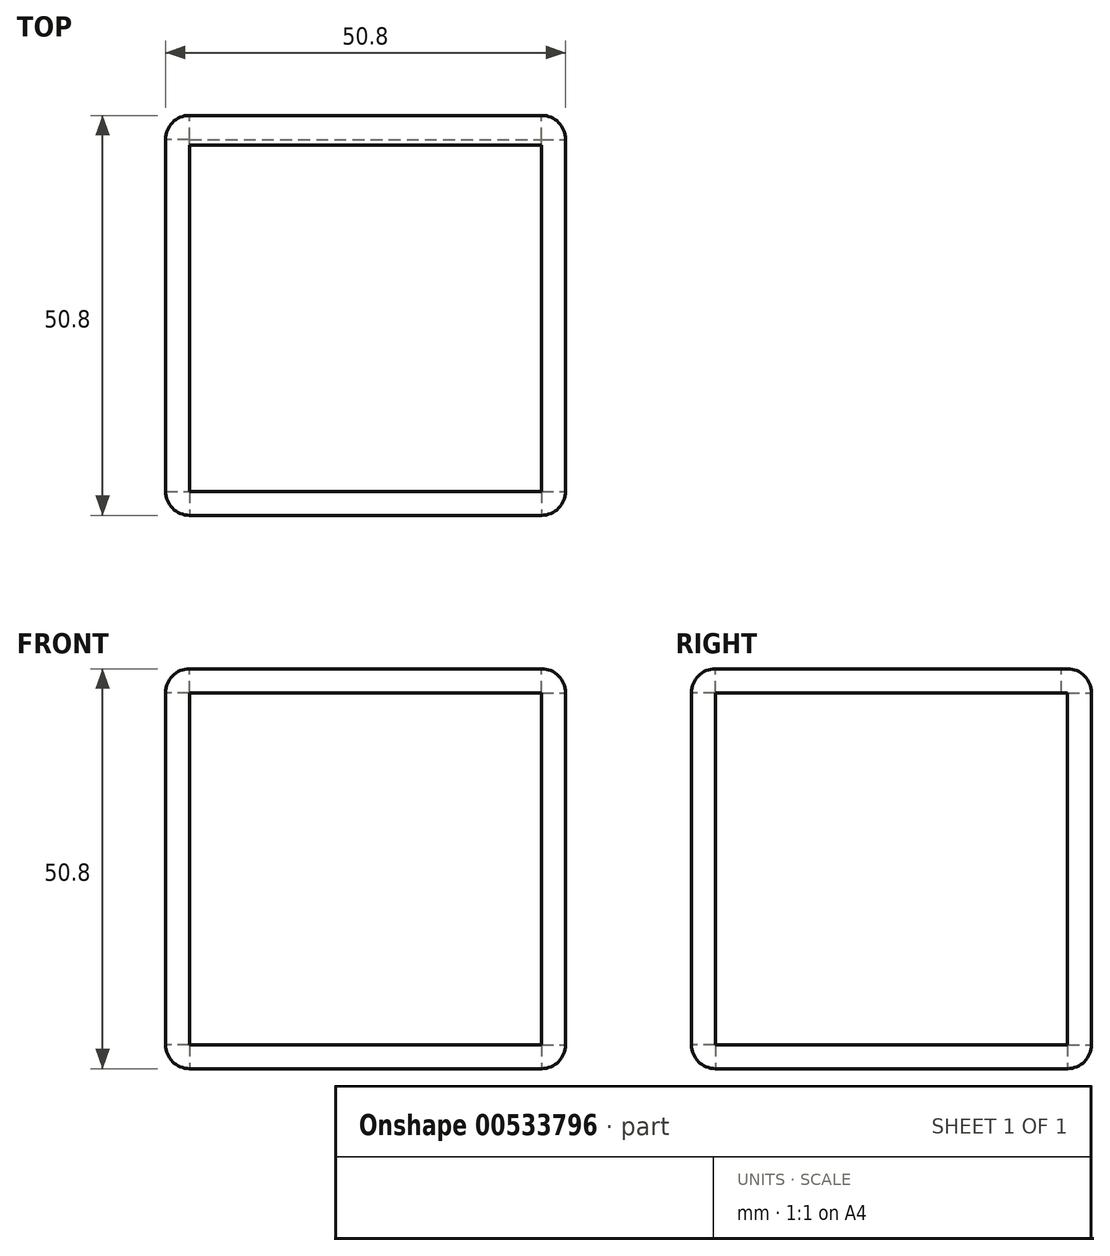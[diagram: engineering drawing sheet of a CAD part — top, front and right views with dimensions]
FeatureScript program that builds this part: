
annotation { "Feature Type Name" : "Feature", "Feature Type Description" : "" }
export const myFeature = defineFeature(function(context is Context, id is Id, definition is map)
    precondition{}
    {
        {
            var Q0;
            Q0=qCreatedBy(makeId("Top.planeOp"),FACE);
            var sketch = newSketch(context, id + "F0", { "sketchPlane" : qUnion([Q0])});
            skLineSegment(sketch, "E0.bottom", {"start": v(0, 0) * mm, "end": v(50.8, 0) * mm});
            skLineSegment(sketch, "E0.top", {"start": v(0, 50.8) * mm, "end": v(50.8, 50.8) * mm});
            skLineSegment(sketch, "E0.left", {"start": v(0, 0) * mm, "end": v(0, 50.8) * mm});
            skLineSegment(sketch, "E0.right", {"start": v(50.8, 0) * mm, "end": v(50.8, 50.8) * mm});
            skLineSegment(sketch, "E1.0", {"start": v(3.05, 47.75) * mm, "end": v(47.75, 47.75) * mm});
            skLineSegment(sketch, "E1.1", {"start": v(3.05, 3.05) * mm, "end": v(3.05, 47.75) * mm});
            skLineSegment(sketch, "E1.2", {"start": v(3.05, 3.05) * mm, "end": v(47.75, 3.05) * mm});
            skLineSegment(sketch, "E1.3", {"start": v(47.75, 3.05) * mm, "end": v(47.75, 47.75) * mm});
            skSolve(sketch);
        }
        {
            var Q0;
            Q0=qCreatedBy(makeId("Front.planeOp"),FACE);
            var sketch = newSketch(context, id + "F1", { "sketchPlane" : qUnion([Q0])});
            skLineSegment(sketch, "E2.bottom", {"start": v(0, 0) * mm, "end": v(50.8, 0) * mm});
            skLineSegment(sketch, "E2.top", {"start": v(0, 50.8) * mm, "end": v(50.8, 50.8) * mm});
            skLineSegment(sketch, "E2.left", {"start": v(0, 0) * mm, "end": v(0, 50.8) * mm});
            skLineSegment(sketch, "E2.right", {"start": v(50.8, 0) * mm, "end": v(50.8, 50.8) * mm});
            skLineSegment(sketch, "E3.0", {"start": v(3.05, 47.75) * mm, "end": v(47.75, 47.75) * mm});
            skLineSegment(sketch, "E3.1", {"start": v(3.05, 3.05) * mm, "end": v(3.05, 47.75) * mm});
            skLineSegment(sketch, "E3.2", {"start": v(3.05, 3.05) * mm, "end": v(47.75, 3.05) * mm});
            skLineSegment(sketch, "E3.3", {"start": v(47.75, 3.05) * mm, "end": v(47.75, 47.75) * mm});
            skSolve(sketch);
        }
        {
            var Q0;
            Q0=qCreatedBy(makeId("Right.planeOp"),FACE);
            var sketch = newSketch(context, id + "F2", { "sketchPlane" : qUnion([Q0])});
            skLineSegment(sketch, "E4.bottom", {"start": v(0, 0) * mm, "end": v(50.8, 0) * mm});
            skLineSegment(sketch, "E4.top", {"start": v(0, 50.8) * mm, "end": v(50.8, 50.8) * mm});
            skLineSegment(sketch, "E4.left", {"start": v(0, 0) * mm, "end": v(0, 50.8) * mm});
            skLineSegment(sketch, "E4.right", {"start": v(50.8, 0) * mm, "end": v(50.8, 50.8) * mm});
            skLineSegment(sketch, "E5.0", {"start": v(3.05, 47.75) * mm, "end": v(47.75, 47.75) * mm});
            skLineSegment(sketch, "E5.1", {"start": v(3.05, 3.05) * mm, "end": v(3.05, 47.75) * mm});
            skLineSegment(sketch, "E5.2", {"start": v(3.05, 3.05) * mm, "end": v(47.75, 3.05) * mm});
            skLineSegment(sketch, "E5.3", {"start": v(47.75, 3.05) * mm, "end": v(47.75, 47.75) * mm});
            skSolve(sketch);
        }
        {
            var Q0;
            Q0=makeQuery(id+"F2.imprint","IMPRINT",FACE,{"disambiguationData":[TD([[makeQuery(id+"F2.imprint","IMPRINT",EDGE,{"derivedFrom":sQuery(id+"F2.wireOp",EDGE,"E5.0")}),-1.0]])]});
            cPlane(context, id + "F3", {"entities" : qUnion([Q0]), "cplaneType" : CPlaneType.OFFSET, "offset" : 50.8 * mm, "width" : 152.4 * mm, "height" : 152.4 * mm});
        }
        {
            var Q0;
            Q0=makeQuery(id+"F1.imprint","IMPRINT",FACE,{"disambiguationData":[TD([[makeQuery(id+"F1.imprint","IMPRINT",EDGE,{"derivedFrom":sQuery(id+"F1.wireOp",EDGE,"E3.0")}),-1.0]])]});
            cPlane(context, id + "F4", {"entities" : qUnion([Q0]), "cplaneType" : CPlaneType.OFFSET, "offset" : 50.8 * mm, "oppositeDirection" : true, "width" : 152.4 * mm, "height" : 152.4 * mm});
        }
        {
            var Q0;
            Q0=makeQuery(id+"F0.imprint","IMPRINT",FACE,{"disambiguationData":[TD([[makeQuery(id+"F0.imprint","IMPRINT",EDGE,{"derivedFrom":sQuery(id+"F0.wireOp",EDGE,"E1.0")}),-1.0]])]});
            cPlane(context, id + "F5", {"entities" : qUnion([Q0]), "cplaneType" : CPlaneType.OFFSET, "offset" : 50.8 * mm, "width" : 152.4 * mm, "height" : 152.4 * mm});
        }
        {
            var Q0;
            Q0=qCreatedBy(id+"F3.planeOp",FACE);
            var sketch = newSketch(context, id + "F6", { "sketchPlane" : qUnion([Q0])});
            skLineSegment(sketch, "E6.bottom", {"start": v(0, 0) * mm, "end": v(50.8, 0) * mm});
            skLineSegment(sketch, "E6.top", {"start": v(0, 50.8) * mm, "end": v(50.8, 50.8) * mm});
            skLineSegment(sketch, "E6.left", {"start": v(0, 0) * mm, "end": v(0, 50.8) * mm});
            skLineSegment(sketch, "E6.right", {"start": v(50.8, 0) * mm, "end": v(50.8, 50.8) * mm});
            skLineSegment(sketch, "E7.0", {"start": v(3.05, 47.75) * mm, "end": v(47.75, 47.75) * mm});
            skLineSegment(sketch, "E7.1", {"start": v(3.05, 3.05) * mm, "end": v(3.05, 47.75) * mm});
            skLineSegment(sketch, "E7.2", {"start": v(3.05, 3.05) * mm, "end": v(47.75, 3.05) * mm});
            skLineSegment(sketch, "E7.3", {"start": v(47.75, 3.05) * mm, "end": v(47.75, 47.75) * mm});
            skSolve(sketch);
        }
        {
            var Q0;
            Q0=qCreatedBy(id+"F4.planeOp",FACE);
            var sketch = newSketch(context, id + "F7", { "sketchPlane" : qUnion([Q0])});
            skLineSegment(sketch, "E8.bottom", {"start": v(0, 0) * mm, "end": v(50.8, 0) * mm});
            skLineSegment(sketch, "E8.top", {"start": v(0, 50.8) * mm, "end": v(50.8, 50.8) * mm});
            skLineSegment(sketch, "E8.left", {"start": v(0, 0) * mm, "end": v(0, 50.8) * mm});
            skLineSegment(sketch, "E8.right", {"start": v(50.8, 0) * mm, "end": v(50.8, 50.8) * mm});
            skLineSegment(sketch, "E9.0", {"start": v(3.05, 47.75) * mm, "end": v(47.75, 47.75) * mm});
            skLineSegment(sketch, "E9.1", {"start": v(3.05, 3.05) * mm, "end": v(3.05, 47.75) * mm});
            skLineSegment(sketch, "E9.2", {"start": v(3.05, 3.05) * mm, "end": v(47.75, 3.05) * mm});
            skLineSegment(sketch, "E9.3", {"start": v(47.75, 3.05) * mm, "end": v(47.75, 47.75) * mm});
            skSolve(sketch);
        }
        {
            var Q0;
            Q0=qCreatedBy(id+"F5.planeOp",FACE);
            var sketch = newSketch(context, id + "F8", { "sketchPlane" : qUnion([Q0])});
            skLineSegment(sketch, "E10.bottom", {"start": v(0, 0) * mm, "end": v(50.8, 0) * mm});
            skLineSegment(sketch, "E10.top", {"start": v(0, 50.04) * mm, "end": v(50.8, 50.04) * mm});
            skLineSegment(sketch, "E10.left", {"start": v(0, 0) * mm, "end": v(0, 50.04) * mm});
            skLineSegment(sketch, "E10.right", {"start": v(50.8, 0) * mm, "end": v(50.8, 50.04) * mm});
            skLineSegment(sketch, "E11.0", {"start": v(3.05, 3.05) * mm, "end": v(47.75, 3.05) * mm});
            skLineSegment(sketch, "E11.1", {"start": v(3.05, 3.05) * mm, "end": v(3.05, 47) * mm});
            skLineSegment(sketch, "E11.2", {"start": v(3.05, 47) * mm, "end": v(47.75, 47) * mm});
            skLineSegment(sketch, "E11.3", {"start": v(47.75, 3.05) * mm, "end": v(47.75, 47) * mm});
            skSolve(sketch);
        }
        {
            var Q0;
            Q0=makeQuery(id+"F0.imprint","IMPRINT",FACE,{"disambiguationData":[TD([[makeQuery(id+"F0.imprint","IMPRINT",EDGE,{"derivedFrom":sQuery(id+"F0.wireOp",EDGE,"E0.bottom")}),1.0]])]});
            extrude(context, id + "F9", {"entities" : qUnion([Q0]), "depth" : 3.05 * mm, "offsetDistance" : 25.4 * mm});
        }
        {
            var Q0;
            Q0=makeQuery(id+"F1.imprint","IMPRINT",FACE,{"disambiguationData":[TD([[makeQuery(id+"F1.imprint","IMPRINT",EDGE,{"derivedFrom":sQuery(id+"F1.wireOp",EDGE,"E2.bottom")}),1.0]])]});
            extrude(context, id + "F10", {"entities" : qUnion([Q0]), "operationType" : NewBodyOperationType.ADD, "oppositeDirection" : true, "depth" : 3.05 * mm, "offsetDistance" : 25.4 * mm});
        }
        {
            var Q0;
            Q0=makeQuery(id+"F2.imprint","IMPRINT",FACE,{"disambiguationData":[TD([[makeQuery(id+"F2.imprint","IMPRINT",EDGE,{"derivedFrom":sQuery(id+"F2.wireOp",EDGE,"E4.bottom")}),1.0]])]});
            extrude(context, id + "F11", {"entities" : qUnion([Q0]), "operationType" : NewBodyOperationType.ADD, "depth" : 3.05 * mm, "offsetDistance" : 25.4 * mm});
        }
        {
            var Q0;
            Q0=makeQuery(id+"F6.imprint","IMPRINT",FACE,{"disambiguationData":[TD([[makeQuery(id+"F6.imprint","IMPRINT",EDGE,{"derivedFrom":sQuery(id+"F6.wireOp",EDGE,"E6.bottom")}),1.0]])]});
            extrude(context, id + "F12", {"entities" : qUnion([Q0]), "operationType" : NewBodyOperationType.ADD, "oppositeDirection" : true, "depth" : 3.05 * mm, "offsetDistance" : 25.4 * mm});
        }
        {
            var Q0;
            Q0=makeQuery(id+"F7.imprint","IMPRINT",FACE,{"disambiguationData":[TD([[makeQuery(id+"F7.imprint","IMPRINT",EDGE,{"derivedFrom":sQuery(id+"F7.wireOp",EDGE,"E8.bottom")}),1.0]])]});
            extrude(context, id + "F13", {"entities" : qUnion([Q0]), "operationType" : NewBodyOperationType.ADD, "depth" : 3.05 * mm, "offsetDistance" : 25.4 * mm});
        }
        {
            var Q0;
            Q0=makeQuery(id+"F8.imprint","IMPRINT",FACE,{"disambiguationData":[TD([[makeQuery(id+"F8.imprint","IMPRINT",EDGE,{"derivedFrom":sQuery(id+"F8.wireOp",EDGE,"E10.bottom")}),1.0]])]});
            extrude(context, id + "F14", {"entities" : qUnion([Q0]), "operationType" : NewBodyOperationType.ADD, "oppositeDirection" : true, "depth" : 3.05 * mm, "offsetDistance" : 25.4 * mm});
        }
        {
            var Q0;
            Q0=makeQuery(id+"F12.boolean.opBoolean","MERGE",EDGE,{"derivedFrom":[makeQuery(id+"F9.opExtrude","SWEPT_EDGE",EDGE,{"disambiguationData":[OSD([sQuery(id+"F0.wireOp",EDGE,"E0.top"),sQuery(id+"F0.wireOp",EDGE,"E0.right")])]}),makeQuery(id+"F12.opExtrude","CAP_EDGE",EDGE,{"disambiguationData":[OSD([sQuery(id+"F6.wireOp",EDGE,"E6.right")])],"isStart":true})]});
            var Q1;
            Q1=makeQuery(id+"F9.opExtrude","CAP_EDGE",EDGE,{"disambiguationData":[OSD([sQuery(id+"F0.wireOp",EDGE,"E0.top")])],"isStart":true});
            var Q2;
            Q2=makeQuery(id+"F9.opExtrude","CAP_EDGE",EDGE,{"disambiguationData":[OSD([sQuery(id+"F0.wireOp",EDGE,"E0.right")])],"isStart":true});
            var Q3;
            Q3=makeQuery(id+"F9.opExtrude","CAP_EDGE",EDGE,{"disambiguationData":[OSD([sQuery(id+"F0.wireOp",EDGE,"E0.bottom")])],"isStart":true});
            var Q4;
            Q4=makeQuery(id+"F10.boolean.opBoolean","MERGE",EDGE,{"derivedFrom":[makeQuery(id+"F9.opExtrude","SWEPT_EDGE",EDGE,{"disambiguationData":[OSD([sQuery(id+"F0.wireOp",EDGE,"E0.bottom"),sQuery(id+"F0.wireOp",EDGE,"E0.right")])]}),makeQuery(id+"F10.opExtrude","CAP_EDGE",EDGE,{"disambiguationData":[OSD([sQuery(id+"F1.wireOp",EDGE,"E2.right")])],"isStart":true})]});
            var Q5;
            Q5=makeQuery(id+"F12.boolean.opBoolean","MERGE",EDGE,{"derivedFrom":[makeQuery(id+"F10.opExtrude","SWEPT_EDGE",EDGE,{"disambiguationData":[OSD([sQuery(id+"F1.wireOp",EDGE,"E2.top"),sQuery(id+"F1.wireOp",EDGE,"E2.right")])]}),makeQuery(id+"F12.opExtrude","CAP_EDGE",EDGE,{"disambiguationData":[OSD([sQuery(id+"F6.wireOp",EDGE,"E6.top")])],"isStart":true})]});
            var Q6;
            Q6=makeQuery(id+"F13.boolean.opBoolean","MERGE",EDGE,{"derivedFrom":[makeQuery(id+"F11.opExtrude","SWEPT_EDGE",EDGE,{"disambiguationData":[OSD([sQuery(id+"F2.wireOp",EDGE,"E4.top"),sQuery(id+"F2.wireOp",EDGE,"E4.right")])]}),makeQuery(id+"F12.opExtrude","SWEPT_EDGE",EDGE,{"disambiguationData":[OSD([sQuery(id+"F6.wireOp",EDGE,"E6.top"),sQuery(id+"F6.wireOp",EDGE,"E6.right")])]}),makeQuery(id+"F13.opExtrude","CAP_EDGE",EDGE,{"disambiguationData":[OSD([sQuery(id+"F7.wireOp",EDGE,"E8.top")])],"isStart":true})]});
            var Q7;
            Q7=makeQuery(id+"F10.opExtrude","CAP_EDGE",EDGE,{"disambiguationData":[OSD([sQuery(id+"F1.wireOp",EDGE,"E2.top")])],"isStart":true});
            var Q8;
            Q8=makeQuery(id+"F11.boolean.opBoolean","MERGE",EDGE,{"derivedFrom":[makeQuery(id+"F10.opExtrude","SWEPT_EDGE",EDGE,{"disambiguationData":[OSD([sQuery(id+"F1.wireOp",EDGE,"E2.top"),sQuery(id+"F1.wireOp",EDGE,"E2.left")])]}),makeQuery(id+"F11.opExtrude","CAP_EDGE",EDGE,{"disambiguationData":[OSD([sQuery(id+"F2.wireOp",EDGE,"E4.top")])],"isStart":true})]});
            var Q9;
            Q9=makeQuery(id+"F11.boolean.opBoolean","MERGE",EDGE,{"derivedFrom":[makeQuery(id+"F9.opExtrude","SWEPT_EDGE",EDGE,{"disambiguationData":[OSD([sQuery(id+"F0.wireOp",EDGE,"E0.top"),sQuery(id+"F0.wireOp",EDGE,"E0.left")])]}),makeQuery(id+"F11.opExtrude","CAP_EDGE",EDGE,{"disambiguationData":[OSD([sQuery(id+"F2.wireOp",EDGE,"E4.right")])],"isStart":true})]});
            var Q10;
            Q10=makeQuery(id+"F9.opExtrude","CAP_EDGE",EDGE,{"disambiguationData":[OSD([sQuery(id+"F0.wireOp",EDGE,"E0.left")])],"isStart":true});
            var Q11;
            Q11=makeQuery(id+"F10.boolean.opBoolean","MERGE",EDGE,{"derivedFrom":[makeQuery(id+"F9.opExtrude","SWEPT_EDGE",EDGE,{"disambiguationData":[OSD([sQuery(id+"F0.wireOp",EDGE,"E0.bottom"),sQuery(id+"F0.wireOp",EDGE,"E0.left")])]}),makeQuery(id+"F10.opExtrude","CAP_EDGE",EDGE,{"disambiguationData":[OSD([sQuery(id+"F1.wireOp",EDGE,"E2.left")])],"isStart":true})]});
            fillet(context, id + "F15", {"entities" : qUnion([Q0, Q1, Q2, Q3, Q4, Q5, Q6, Q7, Q8, Q9, Q10, Q11]), "radius" : 3.05 * mm, "tangentPropagation" : true, "allowEdgeOverflow" : false});
        }
    });
